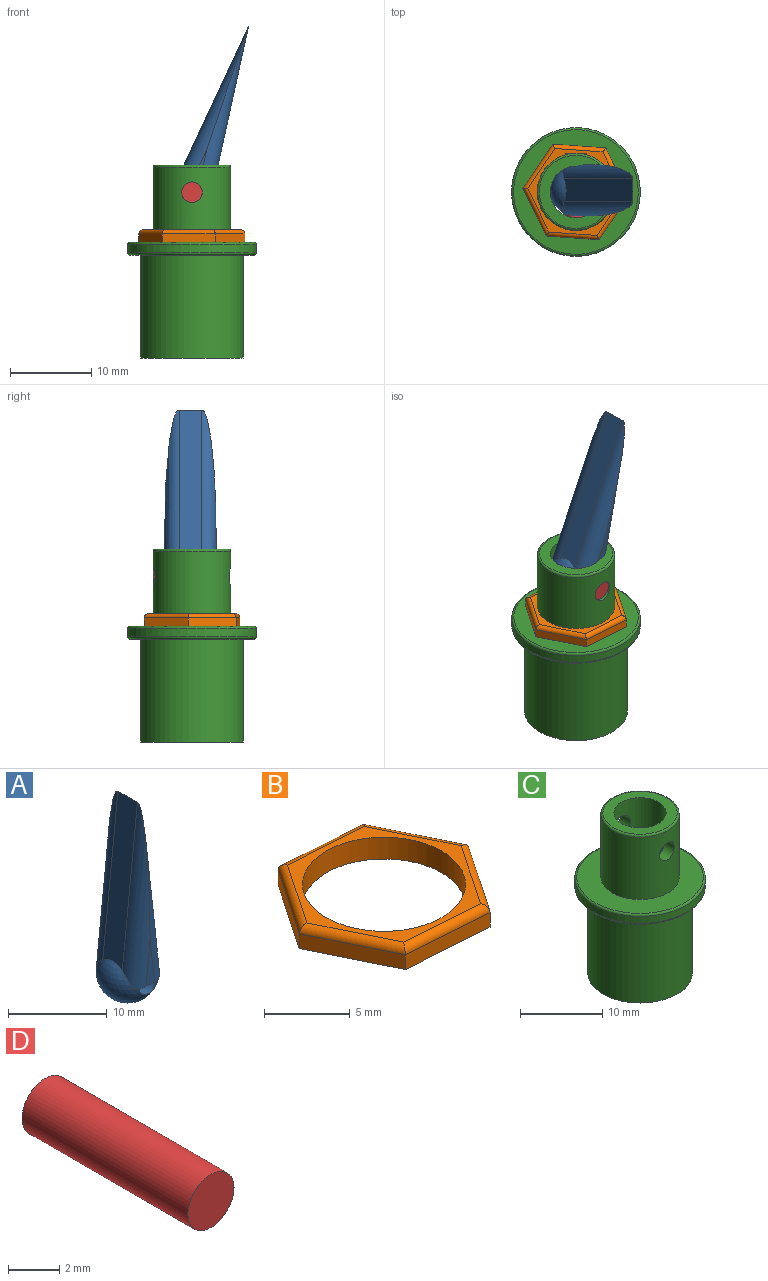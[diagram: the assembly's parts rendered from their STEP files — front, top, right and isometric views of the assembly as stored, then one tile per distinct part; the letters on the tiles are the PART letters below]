
ASSEMBLY  parts=4 mates=3
PART A: 11 faces, bbox 6.4x6.4x24.9 mm
  f0: sphere r=3.17mm, area 78.4mm2, adj f1,f2,f3,f4,f7,f8,f9,f10
  f1: cylinder r=1.27mm len=5.82mm, axis (0,-1,0), area 23.5mm2, adj f0,f2
  f2: plane 6.38x4.26mm, normal (-0.01,0,-1), area 16.4mm2, adj f0,f1,f5,f6,f7,f8,f9,f10
  f3: plane 19.93x2.79mm, normal (0.99,0,0.11), area 55mm2, adj f0,f4,f8,f10
  f4: plane 19.8x2.79mm, normal (-0.99,0,0.11), area 54.6mm2, adj f0,f3,f7,f9
  f5: plane 5.56x1.24mm, normal (0,-1,0), area 3.4mm2, adj f2,f9,f10
  f6: plane 5.56x1.24mm, normal (0,1,0), area 3.4mm2, adj f2,f7,f8
  f7: cylinder r=1.78mm len=21.77mm, axis (-0.11,0,-0.99), area 42.9mm2, adj f0,f2,f4,f6,f8
  f8: cylinder r=1.78mm len=21.83mm, axis (-0.11,0,0.99), area 43.3mm2, adj f0,f2,f3,f6,f7
  f9: cylinder r=1.78mm len=21.77mm, axis (0.11,0,0.99), area 42.9mm2, adj f0,f2,f4,f5,f10
  f10: cylinder r=1.78mm len=21.83mm, axis (0.11,0,-0.99), area 43.3mm2, adj f0,f2,f3,f5,f9
PART B: 15 faces, bbox 13.1x11.8x1.6 mm
  f0: plane 5.89x2.87mm, normal (0.9,0.44,0), area 6.9mm2, adj f1,f6,f8,f10
  f1: plane 6.53x1.05mm, normal (0.07,1,0), area 6.9mm2, adj f0,f2,f8,f9
  f2: plane 5.43x3.67mm, normal (-0.83,0.56,0), area 6.9mm2, adj f1,f3,f8,f11
  f3: plane 5.89x2.87mm, normal (-0.9,-0.44,0), area 6.9mm2, adj f2,f4,f8,f13
  f4: plane 6.53x1.05mm, normal (-0.07,-1,0), area 6.9mm2, adj f3,f6,f8,f14
  f5: cylinder r=4.76mm len=9.53mm, axis (0,0,-1), area 46.6mm2, adj f7,f8
  f6: plane 5.43x3.67mm, normal (0.83,-0.56,0), area 6.9mm2, adj f0,f4,f8,f12
  f7: plane 11.9x10.72mm, normal (0,0,1), area 21.1mm2, adj f5,f9,f10,f11,f12,f13,f14
  f8: plane 13.07x11.78mm, normal (0,0,-1), area 40.2mm2, adj f0,f1,f2,f3,f4,f5,f6
  f9: cylinder r=0.51mm len=6.57mm, axis (1,-0.07,0), area 5.1mm2, adj f1,f7,f10,f11
  f10: cylinder r=0.51mm len=6.11mm, axis (0.44,-0.9,0), area 5.1mm2, adj f0,f7,f9,f12
  f11: cylinder r=0.51mm len=5.71mm, axis (0.56,0.83,0), area 5.1mm2, adj f2,f7,f9,f13
  f12: cylinder r=0.51mm len=5.71mm, axis (-0.56,-0.83,0), area 5.1mm2, adj f6,f7,f10,f14
  f13: cylinder r=0.51mm len=6.11mm, axis (-0.44,0.9,0), area 5.1mm2, adj f3,f7,f11,f14
  f14: cylinder r=0.51mm len=6.57mm, axis (-1,0.07,0), area 5.1mm2, adj f4,f7,f12,f13
PART C: 13 faces, bbox 17.2x17.2x23.8 mm
  f0: cylinder r=1.27mm len=2.54mm, axis (0,1,0), area 13mm2, adj f1,f12
  f1: cylinder r=4.76mm len=9.53mm, axis (0,0,-1), area 267.2mm2, adj f0,f5,f8,f11
  f2: cylinder r=6.35mm len=12.7mm, axis (0,0,1), area 506.7mm2, adj f3,f6
  f3: plane 12.7x12.7mm, normal (0,0,-1), area 95mm2, adj f2,f12
  f4: cylinder r=7.94mm len=15.88mm, axis (0,0,-1), area 52.3mm2, adj f9,f10
  f5: plane 15.37x15.37mm, normal (0,0,1), area 114.2mm2, adj f1,f10
  f6: plane 15.37x15.37mm, normal (0,0,-1), area 58.8mm2, adj f2,f9
  f7: plane 9.02x9.02mm, normal (0,0,1), area 32.2mm2, adj f8,f12
  f8: torus R=4.51mm, axis (0,0,1), area 11.7mm2, adj f1,f7
  f9: torus R=7.68mm, axis (0,0,1), area 19.7mm2, adj f4,f6
  f10: torus R=7.68mm, axis (0,0,1), area 19.7mm2, adj f4,f5
  f11: cylinder r=1.27mm len=2.54mm, axis (0,1,0), area 13mm2, adj f1,f12
  f12: cylinder r=3.17mm len=23.78mm, axis (0,0,1), area 464mm2, adj f0,f3,f7,f11
PART D: 3 faces, bbox 2.5x9.1x2.5 mm
  f0: cylinder r=1.27mm len=9.14mm, axis (0,1,0), area 73mm2, adj f1,f2
  f1: plane 2.54x2.54mm, normal (0,-1,0), area 5.1mm2, adj f0
  f2: plane 2.54x2.54mm, normal (0,1,0), area 5.1mm2, adj f0
PLACE A rot(axis=(0,1,0),18.8deg) t=(12.97,1.85,-0.2)mm
PLACE B t=(12.97,1.65,-6.39)mm
PLACE C t=(12.97,1.65,-7.95)mm fixed
PLACE D t=(12.97,6.42,-0.2)mm
MATE revolute A.f1 <-> D.f0  axis (0,-1,0) through (12.97,1.85,-0.2)mm
MATE fastened B.f5 <-> C.f1  axis (0,0,-1) through (12.97,1.65,-6.39)mm
MATE fastened D.f0 <-> C.f0  axis (0,1,0) through (12.97,6.42,-0.2)mm
